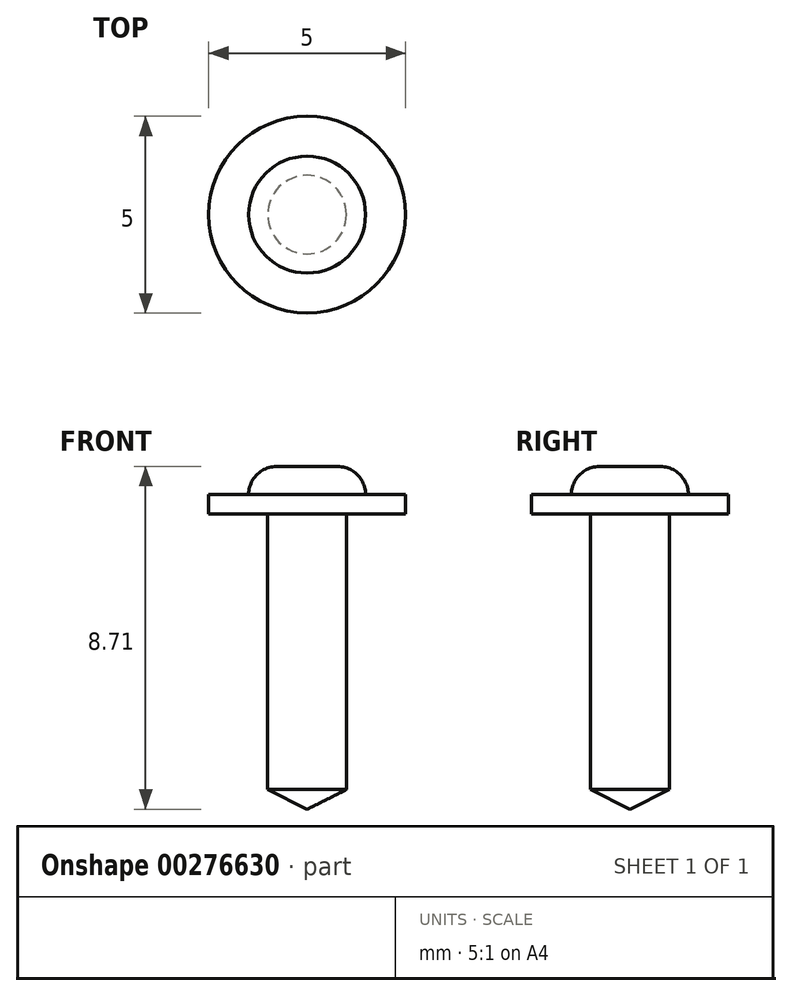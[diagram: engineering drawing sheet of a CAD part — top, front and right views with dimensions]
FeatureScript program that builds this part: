
annotation { "Feature Type Name" : "Feature", "Feature Type Description" : "" }
export const myFeature = defineFeature(function(context is Context, id is Id, definition is map)
    precondition{}
    {
        {
            var Q0;
            Q0=qCreatedBy(makeId("Front.planeOp"),FACE);
            var sketch = newSketch(context, id + "F0", { "sketchPlane" : qUnion([Q0])});
            skLineSegment(sketch, "E0", {"start": v(0, 0) * mm, "end": v(0, -7.5) * mm});
            skLineSegment(sketch, "E1", {"start": v(0, -7.5) * mm, "end": v(1, -7) * mm});
            skLineSegment(sketch, "E2", {"start": v(1, -7) * mm, "end": v(1, 0) * mm});
            skLineSegment(sketch, "E3", {"start": v(1, 0) * mm, "end": v(2.5, 0) * mm});
            skLineSegment(sketch, "E4", {"start": v(2.5, 0) * mm, "end": v(2.5, 0.5) * mm});
            skLineSegment(sketch, "E5", {"start": v(2.5, 0.5) * mm, "end": v(1.48, 0.5) * mm});
            skLineSegment(sketch, "E6", {"start": v(1.48, 0.5) * mm, "end": v(0, 0.5) * mm, "construction": true});
            skLineSegment(sketch, "E7", {"start": v(0, 0.5) * mm, "end": v(0, 0) * mm});
            skLineSegment(sketch, "E8", {"start": v(0, 0.5) * mm, "end": v(0, 1.2) * mm});
            skLineSegment(sketch, "E9", {"start": v(0, 1.2) * mm, "end": v(0.78, 1.2) * mm});
            skArc(sketch, "E10", {"start": v(1.48, 0.5) * mm, "mid": v(1.28, 1) * mm, "end": v(0.78, 1.2) * mm});
            skSolve(sketch);
        }
        {
            var Q0;
            Q0 = qSketchRegion(id + "F0", true);
            var Q1;
            Q1=sQuery(id+"F0.wireOp",EDGE,"E0");
            revolve(context, id + "F1", {"entities" : qUnion([Q0]), "axis" : qUnion([Q1]), "revolveType" : RevolveType.FULL});
        }
    });
